# Revit family: bottle _filling_station_ mechanically_activated_bi-level_elkay-EMABFTLDDLC
name_source: partatom
category: Plumbing Fixtures
units: mm (PartAtom-declared; Revit-internal decimal feet)

## family parameters
Always vertical = Yes
Cut with Voids When Loaded = No
Maintain Annotation Orientation = No
OmniClass Number = 23.65.70.14.11
OmniClass Title = Drinking Fountains/Coolers
Part Type = Normal
Room Calculation Point = No
Round Connector Dimension = Use Diameter
Shared = No
Work Plane-Based = No

## types (1)
- EMABFTLDDLC (Wall Mount Mechanical Activation Bi-level ADA Cooler)
    Activation Method = Mechanical Front and Side Bubbler Pushbar
    Approx. Shipping Weight (lbs) = 46
    Assembly Code = D2010800
    CWFU = 0
    Chilling Capacity (GPH) = 8
    Current = 0 A
    Default Elevation = 0 "
    Description = Wall Mount Mechanical Activation Bi-level ADA Cooler Non-filtered Non-refrigerated Light Gray Granite
    Dimensions (L x W x H) = "36 1/4 inch x 18 5/8 inch x 27 inch"
    Electrical connection Height from floor level = 25.125 "
    HWFU = 0
    Hieght = 46.25 "
    Inlet Connection Size (inch) = 0.375 "
    Inlet connection Height from floor level = 20.125 "
    Installation Location = Wall Mount (On Wall)
    Length = 36.25 "
    Main Material = Elkay-Finish-Light gray
    Manufacturer = Elkay Manufacturer Company
    Manufacturer Brand = Elkay (by Zurn Elkay Water Solutions)
    Masking R1 = 0.25 "
    Material_Water cooler = Elkay-Finish-Black
    Model = EMABFTLDDLC
    Mounting Type = Indoor
    Number of Poles = 1
    Outlet Connection Size (inch) = 1.5 "
    Outlet connection = 18.75 "
    Power Factor = 1
    Product Documentation Link = https://www.elkayfiles.com
    Product Installation Sheet URL = https://www.elkayfiles.com
    Product Page URL = https://www.elkay.com
    Product Weight (lbs) = 36
    Product data URL = https://bimobject.com
    Repair Parts URL = https://www.elkayfiles.com
    URL = https://www.elkay.com
    Voltage = 115 V
    WFU = 0
    Width = 18.625 "

## geometry (parser evidence)
native form markers: Sweep x10
no freeform markers — native parametric forms only
